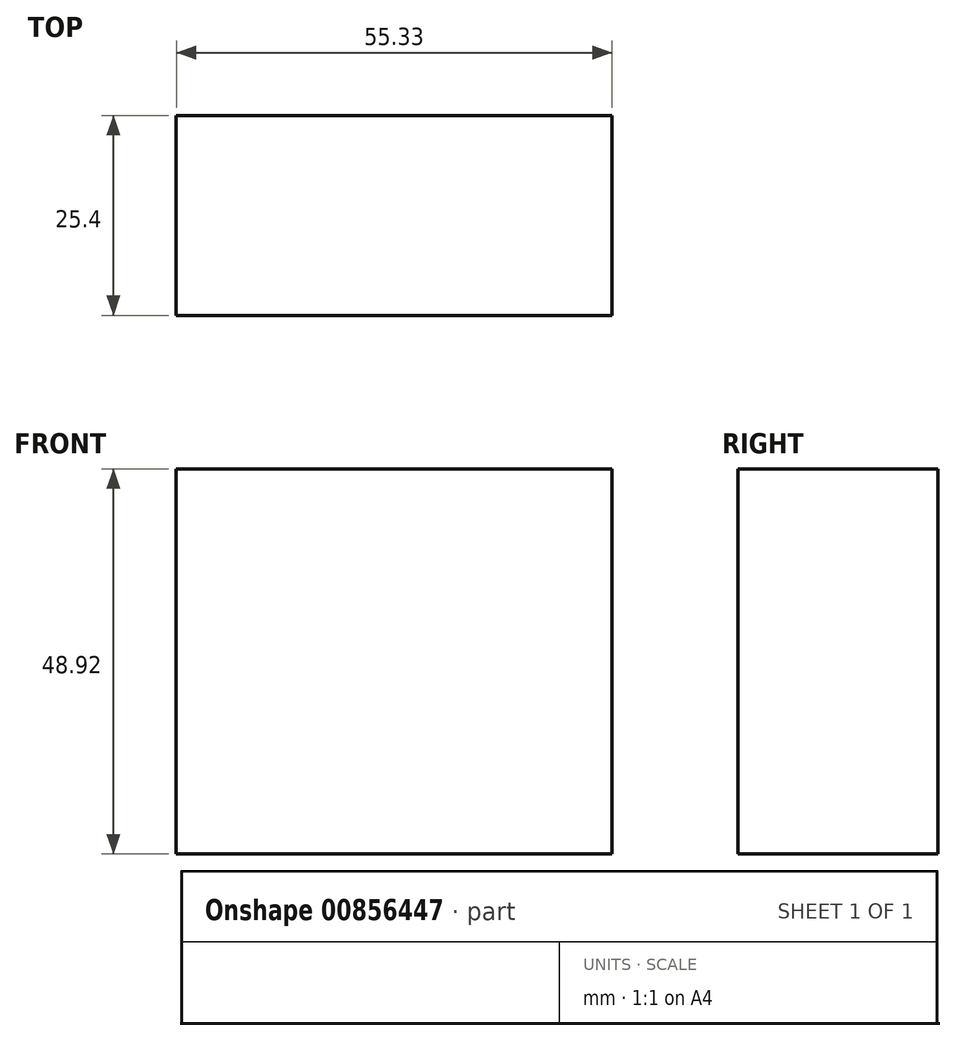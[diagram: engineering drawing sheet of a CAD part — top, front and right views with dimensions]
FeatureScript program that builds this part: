
annotation { "Feature Type Name" : "Feature", "Feature Type Description" : "" }
export const myFeature = defineFeature(function(context is Context, id is Id, definition is map)
    precondition{}
    {
        {
            var Q0;
            Q0=qCreatedBy(makeId("Front.planeOp"),FACE);
            var sketch = newSketch(context, id + "F0", { "sketchPlane" : qUnion([Q0])});
            skLineSegment(sketch, "E0.bottom", {"start": v(-127.61, 30.8) * mm, "end": v(-72.28, 30.8) * mm});
            skLineSegment(sketch, "E0.top", {"start": v(-127.61, -18.11) * mm, "end": v(-72.28, -18.11) * mm});
            skLineSegment(sketch, "E0.left", {"start": v(-127.61, 30.8) * mm, "end": v(-127.61, -18.11) * mm});
            skLineSegment(sketch, "E0.right", {"start": v(-72.28, 30.8) * mm, "end": v(-72.28, -18.11) * mm});
            skSolve(sketch);
        }
        {
            var Q0;
            Q0 = qSketchRegion(id + "F0", true);
            extrude(context, id + "F1", {"entities" : qUnion([Q0]), "depth" : 25.4 * mm, "offsetDistance" : 25.4 * mm});
        }
    });
